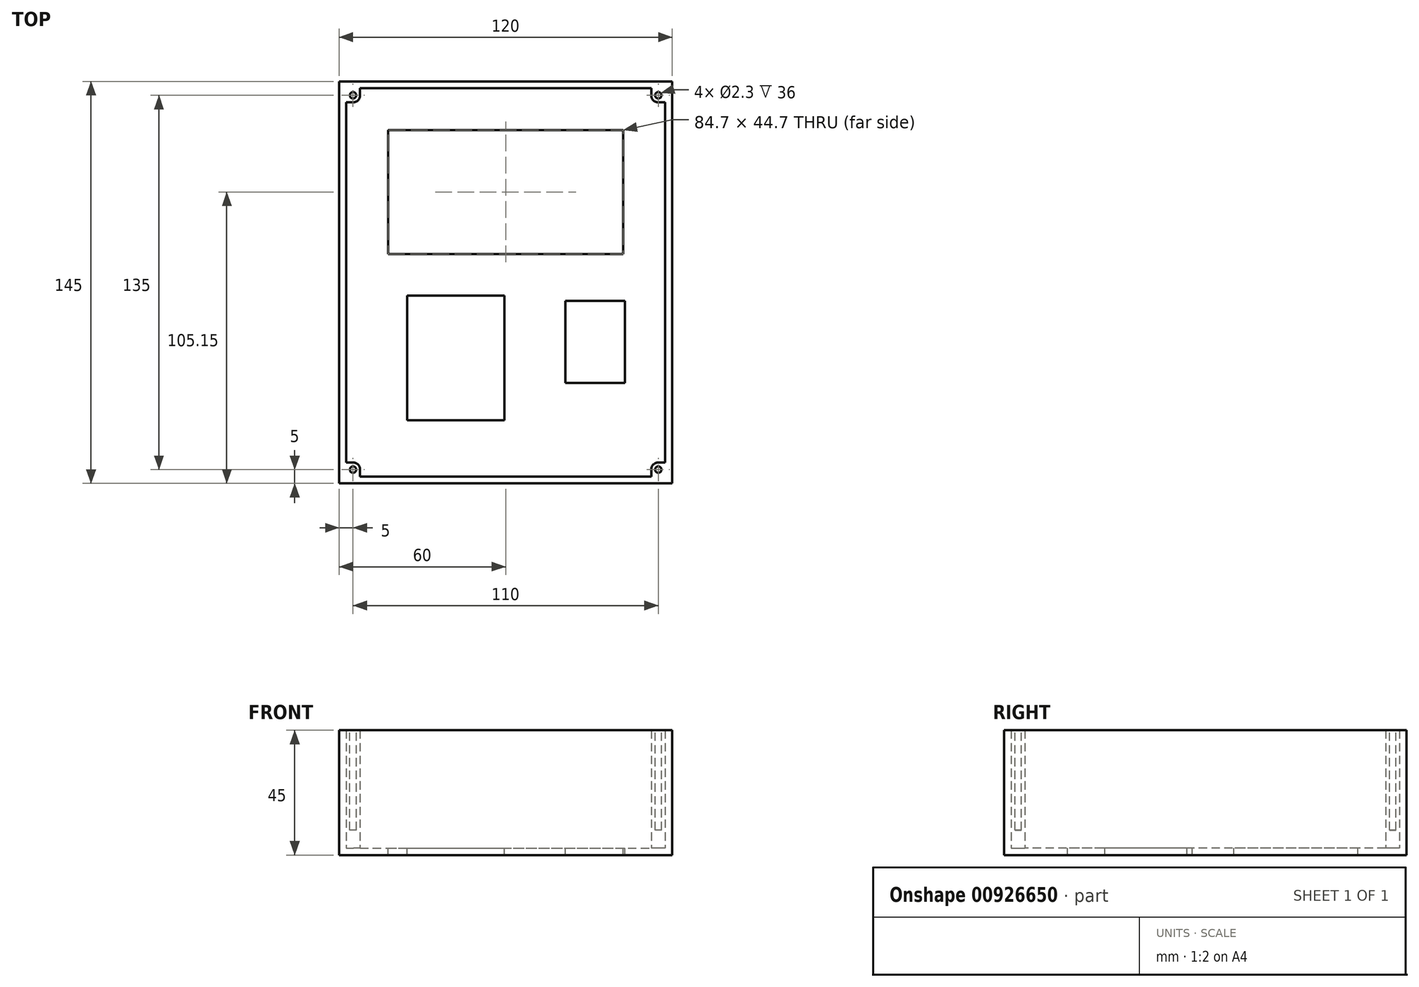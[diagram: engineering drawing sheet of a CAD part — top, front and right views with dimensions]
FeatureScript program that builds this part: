
annotation { "Feature Type Name" : "Feature", "Feature Type Description" : "" }
export const myFeature = defineFeature(function(context is Context, id is Id, definition is map)
    precondition{}
    {
        {
            assignVariable(context, id + "F0", {"name" : "depth", "anyValue" : 45});
        }
        {
            assignVariable(context, id + "F1", {"name" : "shell", "anyValue" : 2.5});
        }
        {
            assignVariable(context, id + "F2", {"name" : "bottom_screw_depth", "anyValue" : getVariable(context, 'depth') * 0.8});
        }
        {
            assignVariable(context, id + "F3", {"name" : "bottom_screw_hole", "anyValue" : 2.3});
        }
        {
            var Q0;
            Q0=qCreatedBy(makeId("Top.planeOp"),FACE);
            var sketch = newSketch(context, id + "F4", { "sketchPlane" : qUnion([Q0])});
            skLineSegment(sketch, "E0.bottom", {"start": v(-60, 72.5) * mm, "end": v(60, 72.5) * mm});
            skLineSegment(sketch, "E0.top", {"start": v(-60, -72.5) * mm, "end": v(60, -72.5) * mm});
            skLineSegment(sketch, "E0.left", {"start": v(-60, 72.5) * mm, "end": v(-60, -72.5) * mm});
            skLineSegment(sketch, "E0.right", {"start": v(60, 72.5) * mm, "end": v(60, -72.5) * mm});
            skSolve(sketch);
        }
        {
            var Q0;
            Q0 = qSketchRegion(id + "F4", true);
            extrude(context, id + "F5", {"entities" : qUnion([Q0]), "depth" : (getVariable(context, 'depth')) * mm, "offsetDistance" : 25 * mm});
        }
        {
            var Q0;
            Q0=makeQuery(id+"F5.opExtrude","CAP_FACE",FACE,{"disambiguationData":[OSD([sQuery(id+"F4.wireOp",EDGE,"E0.bottom"),sQuery(id+"F4.wireOp",EDGE,"E0.top"),sQuery(id+"F4.wireOp",EDGE,"E0.left"),sQuery(id+"F4.wireOp",EDGE,"E0.right")])],"isStart":false});
            shell(context, id + "F6", {"entities" : qUnion([Q0]), "thickness" : (getVariable(context, 'shell')) * mm});
        }
        {
            var Q0;
            Q0=makeQuery(id+"F6.opShell","OFFSET_FACE",FACE,{"disambiguationData":[OSD([sQuery(id+"F4.wireOp",EDGE,"E0.bottom"),sQuery(id+"F4.wireOp",EDGE,"E0.top"),sQuery(id+"F4.wireOp",EDGE,"E0.left"),sQuery(id+"F4.wireOp",EDGE,"E0.right")])]});
            var sketch = newSketch(context, id + "F7", { "sketchPlane" : qUnion([Q0])});
            skLineSegment(sketch, "E1.bottom", {"start": v(-42.35, 55) * mm, "end": v(42.35, 55) * mm});
            skLineSegment(sketch, "E1.top", {"start": v(-42.35, 10.3) * mm, "end": v(42.35, 10.3) * mm});
            skLineSegment(sketch, "E1.left", {"start": v(-42.35, 55) * mm, "end": v(-42.35, 10.3) * mm});
            skLineSegment(sketch, "E1.right", {"start": v(42.35, 55) * mm, "end": v(42.35, 10.3) * mm});
            skSolve(sketch);
        }
        {
            var Q0;
            Q0=makeQuery(id+"F7.imprint","IMPRINT",FACE,{"disambiguationData":[TD([[makeQuery(id+"F7.imprint","IMPRINT",EDGE,{"derivedFrom":sQuery(id+"F7.wireOp",EDGE,"E1.bottom")}),1.0]])]});
            var sketch = newSketch(context, id + "F8", { "sketchPlane" : qUnion([Q0])});
            skLineSegment(sketch, "E2.bottom", {"start": v(-35.5, -4.7) * mm, "end": v(-0.5, -4.7) * mm});
            skLineSegment(sketch, "E2.top", {"start": v(-35.5, -49.7) * mm, "end": v(-0.5, -49.7) * mm});
            skLineSegment(sketch, "E2.left", {"start": v(-35.5, -4.7) * mm, "end": v(-35.5, -49.7) * mm});
            skLineSegment(sketch, "E2.right", {"start": v(-0.5, -4.7) * mm, "end": v(-0.5, -49.7) * mm});
            skLineSegment(sketch, "E3", {"start": v(21.5, 0) * mm, "end": v(21.5, -49.7) * mm, "construction": true});
            skLineSegment(sketch, "E4.bottom", {"start": v(21.5, -6.62) * mm, "end": v(43, -6.62) * mm});
            skLineSegment(sketch, "E4.top", {"start": v(21.5, -36.22) * mm, "end": v(43, -36.22) * mm});
            skLineSegment(sketch, "E4.left", {"start": v(21.5, -6.62) * mm, "end": v(21.5, -36.22) * mm});
            skLineSegment(sketch, "E4.right", {"start": v(43, -6.62) * mm, "end": v(43, -36.22) * mm});
            skSolve(sketch);
        }
        {
            var Q0;
            Q0 = qSketchRegion(id + "F8", true);
            var Q1;
            Q1 = qSketchRegion(id + "F7", true);
            extrude(context, id + "F9", {"entities" : qUnion([Q0, Q1]), "operationType" : NewBodyOperationType.REMOVE, "oppositeDirection" : true, "depth" : (getVariable(context, 'shell')) * mm, "offsetDistance" : 25 * mm});
        }
        {
            var Q0;
            Q0=makeQuery(id+"F6.opShell","OFFSET_FACE",FACE,{"disambiguationData":[OSD([sQuery(id+"F4.wireOp",EDGE,"E0.bottom"),sQuery(id+"F4.wireOp",EDGE,"E0.top"),sQuery(id+"F4.wireOp",EDGE,"E0.left"),sQuery(id+"F4.wireOp",EDGE,"E0.right")])]});
            var sketch = newSketch(context, id + "F10", { "sketchPlane" : qUnion([Q0])});
            skLineSegment(sketch, "E5.bottom", {"start": v(-57.5, 70) * mm, "end": v(-52.5, 70) * mm});
            skLineSegment(sketch, "E5.top", {"start": v(-57.5, 65) * mm, "end": v(-52.5, 65) * mm});
            skLineSegment(sketch, "E5.left", {"start": v(-57.5, 70) * mm, "end": v(-57.5, 65) * mm});
            skLineSegment(sketch, "E5.right", {"start": v(-52.5, 70) * mm, "end": v(-52.5, 65) * mm});
            skLineSegment(sketch, "E6.bottom", {"start": v(57.5, 70) * mm, "end": v(52.5, 70) * mm});
            skLineSegment(sketch, "E6.top", {"start": v(57.5, 65) * mm, "end": v(52.5, 65) * mm});
            skLineSegment(sketch, "E6.left", {"start": v(57.5, 70) * mm, "end": v(57.5, 65) * mm});
            skLineSegment(sketch, "E6.right", {"start": v(52.5, 70) * mm, "end": v(52.5, 65) * mm});
            skLineSegment(sketch, "E7.bottom", {"start": v(57.5, -70) * mm, "end": v(52.5, -70) * mm});
            skLineSegment(sketch, "E7.top", {"start": v(57.5, -65) * mm, "end": v(52.5, -65) * mm});
            skLineSegment(sketch, "E7.left", {"start": v(57.5, -70) * mm, "end": v(57.5, -65) * mm});
            skLineSegment(sketch, "E7.right", {"start": v(52.5, -70) * mm, "end": v(52.5, -65) * mm});
            skLineSegment(sketch, "E8.bottom", {"start": v(-57.5, -70) * mm, "end": v(-52.5, -70) * mm});
            skLineSegment(sketch, "E8.top", {"start": v(-57.5, -65) * mm, "end": v(-52.5, -65) * mm});
            skLineSegment(sketch, "E8.left", {"start": v(-57.5, -70) * mm, "end": v(-57.5, -65) * mm});
            skLineSegment(sketch, "E8.right", {"start": v(-52.5, -70) * mm, "end": v(-52.5, -65) * mm});
            skSolve(sketch);
        }
        {
            var Q0;
            Q0=makeQuery(id+"F10.imprint","IMPRINT",FACE,{"disambiguationData":[TD([[makeQuery(id+"F10.imprint","IMPRINT",EDGE,{"derivedFrom":sQuery(id+"F10.wireOp",EDGE,"E5.bottom")}),-1.0]])]});
            var Q1;
            Q1=makeQuery(id+"F10.imprint","IMPRINT",FACE,{"disambiguationData":[TD([[makeQuery(id+"F10.imprint","IMPRINT",EDGE,{"derivedFrom":sQuery(id+"F10.wireOp",EDGE,"E8.bottom")}),1.0]])]});
            var Q2;
            Q2=makeQuery(id+"F10.imprint","IMPRINT",FACE,{"disambiguationData":[TD([[makeQuery(id+"F10.imprint","IMPRINT",EDGE,{"derivedFrom":sQuery(id+"F10.wireOp",EDGE,"E7.bottom")}),1.0]])]});
            var Q3;
            Q3=makeQuery(id+"F10.imprint","IMPRINT",FACE,{"disambiguationData":[TD([[makeQuery(id+"F10.imprint","IMPRINT",EDGE,{"derivedFrom":sQuery(id+"F10.wireOp",EDGE,"E6.bottom")}),-1.0]])]});
            extrude(context, id + "F11", {"entities" : qUnion([Q0, Q1, Q2, Q3]), "operationType" : NewBodyOperationType.ADD, "depth" : (getVariable(context, 'depth') - getVariable(context, 'shell')) * mm, "offsetDistance" : 25 * mm});
        }
        {
            var Q0;
            Q0=makeQuery(id+"F11.boolean.opBoolean","MERGE",FACE,{"derivedFrom":[makeQuery(id+"F5.opExtrude","CAP_FACE",FACE,{"disambiguationData":[OSD([sQuery(id+"F4.wireOp",EDGE,"E0.bottom"),sQuery(id+"F4.wireOp",EDGE,"E0.top"),sQuery(id+"F4.wireOp",EDGE,"E0.left"),sQuery(id+"F4.wireOp",EDGE,"E0.right")])],"isStart":false}),makeQuery(id+"F11.opExtrude","CAP_FACE",FACE,{"disambiguationData":[OSD([sQuery(id+"F10.wireOp",EDGE,"E5.bottom"),sQuery(id+"F10.wireOp",EDGE,"E5.top"),sQuery(id+"F10.wireOp",EDGE,"E5.left"),sQuery(id+"F10.wireOp",EDGE,"E5.right")])],"isStart":false})]});
            var sketch = newSketch(context, id + "F12", { "sketchPlane" : qUnion([Q0])});
            skLineSegment(sketch, "E9", {"start": v(-52.5, 65) * mm, "end": v(-60, 72.5) * mm, "construction": true});
            skLineSegment(sketch, "E10", {"start": v(-57.5, 65) * mm, "end": v(-52.5, 70) * mm, "construction": true});
            skCircle(sketch, "E11", {"center": v(-55, 67.5) * mm, "radius": 1.15 * mm});
            skLineSegment(sketch, "E12", {"start": v(-57.5, -65) * mm, "end": v(-52.5, -70) * mm, "construction": true});
            skLineSegment(sketch, "E13", {"start": v(-52.5, -65) * mm, "end": v(-60, -72.5) * mm, "construction": true});
            skCircle(sketch, "E14", {"center": v(-55, -67.5) * mm, "radius": 1.15 * mm});
            skLineSegment(sketch, "E15", {"start": v(52.5, -70) * mm, "end": v(57.5, -65) * mm, "construction": true});
            skLineSegment(sketch, "E16", {"start": v(52.5, -65) * mm, "end": v(60, -72.5) * mm, "construction": true});
            skCircle(sketch, "E17", {"center": v(55, -67.5) * mm, "radius": 1.15 * mm});
            skPoint(sketch, "E17.perimeterSnap0", {"position": v(55, -67.5) * mm});
            skPoint(sketch, "E17.perimeterSnap1", {"position": v(56.25, -68.75) * mm});
            skLineSegment(sketch, "E18", {"start": v(52.5, 65) * mm, "end": v(60, 72.5) * mm, "construction": true});
            skLineSegment(sketch, "E19", {"start": v(52.5, 70) * mm, "end": v(57.5, 65) * mm, "construction": true});
            skCircle(sketch, "E20", {"center": v(55, 67.5) * mm, "radius": 1.15 * mm});
            skSolve(sketch);
        }
        {
            var Q0;
            Q0=makeQuery(id+"F12.imprint","IMPRINT",FACE,{"disambiguationData":[TD([[makeQuery(id+"F12.imprint","IMPRINT",EDGE,{"derivedFrom":sQuery(id+"F12.wireOp",EDGE,"E11")}),1.0]])]});
            var Q1;
            Q1=makeQuery(id+"F12.imprint","IMPRINT",FACE,{"disambiguationData":[TD([[makeQuery(id+"F12.imprint","IMPRINT",EDGE,{"derivedFrom":sQuery(id+"F12.wireOp",EDGE,"E20")}),1.0]])]});
            var Q2;
            Q2=makeQuery(id+"F12.imprint","IMPRINT",FACE,{"disambiguationData":[TD([[makeQuery(id+"F12.imprint","IMPRINT",EDGE,{"derivedFrom":sQuery(id+"F12.wireOp",EDGE,"E17")}),1.0]])]});
            var Q3;
            Q3=makeQuery(id+"F12.imprint","IMPRINT",FACE,{"disambiguationData":[TD([[makeQuery(id+"F12.imprint","IMPRINT",EDGE,{"derivedFrom":sQuery(id+"F12.wireOp",EDGE,"E14")}),1.0]])]});
            extrude(context, id + "F13", {"entities" : qUnion([Q0, Q1, Q2, Q3]), "operationType" : NewBodyOperationType.REMOVE, "oppositeDirection" : true, "depth" : (getVariable(context, 'bottom_screw_depth')) * mm, "offsetDistance" : 25 * mm});
        }
        {
            var Q0;
            Q0=makeQuery(id+"F11.opExtrude","SWEPT_EDGE",EDGE,{"disambiguationData":[OSD([sQuery(id+"F10.wireOp",EDGE,"E5.top"),sQuery(id+"F10.wireOp",EDGE,"E5.right")])]});
            var Q1;
            Q1=makeQuery(id+"F11.opExtrude","SWEPT_EDGE",EDGE,{"disambiguationData":[OSD([sQuery(id+"F10.wireOp",EDGE,"E6.top"),sQuery(id+"F10.wireOp",EDGE,"E6.right")])]});
            var Q2;
            Q2=makeQuery(id+"F11.opExtrude","SWEPT_EDGE",EDGE,{"disambiguationData":[OSD([sQuery(id+"F10.wireOp",EDGE,"E7.top"),sQuery(id+"F10.wireOp",EDGE,"E7.right")])]});
            var Q3;
            Q3=makeQuery(id+"F11.opExtrude","SWEPT_EDGE",EDGE,{"disambiguationData":[OSD([sQuery(id+"F10.wireOp",EDGE,"E8.top"),sQuery(id+"F10.wireOp",EDGE,"E8.right")])]});
            fillet(context, id + "F14", {"entities" : qUnion([Q0, Q1, Q2, Q3]), "radius" : (getVariable(context, 'bottom_screw_hole')) * mm, "tangentPropagation" : true, "allowEdgeOverflow" : false});
        }
    });
